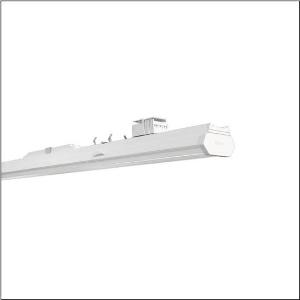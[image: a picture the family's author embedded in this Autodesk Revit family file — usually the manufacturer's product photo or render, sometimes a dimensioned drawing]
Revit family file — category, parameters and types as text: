
# Revit family: licross_11_protected_mo_51tp11dn59xg
name_source: partatom
category: Lighting Fixtures
units: mm (PartAtom-declared; Revit-internal decimal feet)

## family parameters
Cut with Voids When Loaded = No
Host = Face
Light Source = No
Part Type = Normal
Room Calculation Point = No
Round Connector Dimension = Use Diameter
Shared = No

## types (1)
- --- (1 x LED, 9100 lm, 52.7 W, 5000K)
    Apparent Load = 53 VA
    CIE Flux Codes = 83 94 98 100 100
    Color Rendering = 80
    Color Temperature = 5000K
    Default Elevation = 1800 mm
    Description = Licross 11 Protected MO, luminaire insert, of sheet steel, galvanised, coil coated, white, length: 1.500mm, width: 90mm, height: 101mm, LED rated luminous flux: 9.100lm, light colour: 850, SDCM (Standard Deviation of Colour Matching)MacAdam ≤ 2 SDCM (initial), control gear: DALI 2, with plug, 5-pole, with phase selection, mains connection: 220..240V, AC, 50/60Hz, rated input power: 53W, internal wiring halogen-free, primary light control with lens, of plastic, primary optical cover: cover, of PMMA, light emission: direct distribution, primary light characteristic: symmetric, protection rating (complete): IP64, insulation class (complete): insulation class I (protective earthing), certification: CE, ENEC, VDE, UKCA, protection symbol: D if used in an environment with conductive dust loads with corresponding accessories, impact resistance: IK06, permissible ambient temperature for indoor applications: -25..+35°C, LABS conformity tested according to VDMA 24364:2018-05, reducing of maximum allowable ambient temperature of 5°C with ceiling mounting, corresponds to IFS (International Featured Standards) requirements for safety and quality in the food industry, The light source and the operating device comply with the requirements of the Ecodesign Regulation (EU) 2019/2020 and are replaceable in accordance with this regulation, packaging unit: 1 piece
    Height = 92 mm
    Lamp = 1 x LED
    Lamp Light Flux = 9100 lm
    Lamp Power = 52.7 W
    Lamp count = 1
    Length = 1500 mm
    Luminous efficacy = 173 lm/W
    Manufacturer = Siteco
    ModVariant = No
    Model = 51TP11DN59XG
    Mounting Place = Ceiling
    Mounting Type = Pendant
    Number of Poles = 1
    OnlyDefault = Yes
    Power Factor = 1
    Product Name = Licross 11 Protected MO
    Product group = luminaire insert | ceiling pendant
    ProductGroupID = 901
    Protection Class = Protection class I
    Protection Degree = IP 64
    RLX_Detail_Level = 1
    RLX_Emergency_Light_Flux = 0 lm
    RLX_Emergency_Type = 0
    RLX_Emergency_Type_DB = No
    RlxData = <blob elided: 24397 chars, md5=69c985f2>
    Socket = socket
    Standby Power = 0 W
    System Light Flux = 9100 lm
    System Power = 53 W
    Type Comments = factory setting: luminous flux: 100 % | dim-lin: 254 | 350 mA
    Type Image = l_1256148.jpg
    URL = http://relux.com
    VarID = @adj_021059
    Voltage = 0 V
    Weight = 0.00 kg
    Width = 88 mm

## geometry (parser evidence)
native form markers: Blend x4, Sweep x10
no freeform markers — native parametric forms only
